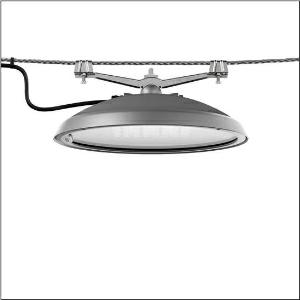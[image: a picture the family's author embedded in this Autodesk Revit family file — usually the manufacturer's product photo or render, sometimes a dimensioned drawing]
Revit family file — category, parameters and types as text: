
# Revit family: dl_r__50_iq_mini___st1_0s_5xa248w41f08he_3a14
name_source: partatom
category: Lighting Fixtures
units: mm (PartAtom-declared; Revit-internal decimal feet)

## family parameters
Cut with Voids When Loaded = No
Host = Face
Light Source = No
Part Type = Normal
Room Calculation Point = No
Round Connector Dimension = Use Diameter
Shared = No

## types (1)
- --- (1 x LED, 9400 lm, 64.6 W, 4000K)
    Apparent Load = 65 VA
    CIE Flux Codes = 37 72 97 100 100
    Color Rendering = 70
    Color Temperature = 4000K
    Default Elevation = 1800 mm
    Description = DL® 50 iQ mini, catenary luminaire, primary light control with lens, of PMMA, primary optical cover: cover, of toughened safety glass, transparent, light distribution: ST1.0s, light emission: direct distribution, primary light characteristic: symmetric, installation type: suspended mounting, LED, High Power LED, rated luminous flux: 9.400lm, luminous efficacy: 146lm/W, light colour: 740, colour temperature: 4000K, control: optimised constant luminous flux control (CLO 2.0), Desk-Remote (wireless, voltage-free reading and setting of iQ features in the workshop via application-optimized NFC function/RFID function), Light-Fading, Smart-Wire, Night-Set, Lumen-Switch, Temp-Guard, Auto-Match, Street-Remote, mains connection: 230..240V, AC, 50/60Hz, start of lifetime: 65W, end of service life: 68W, reduction: 29W, luminaire housing, of diecast aluminium, powder-coated, Siteco® metallic grey (DB 702S), diameter: 500mm, height: 115mm, protection rating (complete): IP66, insulation class (complete): insulation class II (safety insulation), certification: CE, ENEC, VDE, impact resistance: IK08, permissible operating ambient temperature for outdoor applications: -25..+40°C, standard-compliant lighting for roads and squares, packaging unit: 1 piece

Light Distribution: ST1.0s
    Height = 124 mm  [stored 0.406824 ft]
    Lamp = 1 x LED
    Lamp Light Flux = 9400 lm
    Lamp Power = 64.6 W
    Lamp count = 1
    Length = 500 mm
    Luminous efficacy = 146 lm/W
    Manufacturer = Siteco
    ModVariant = No
    Model = 5XA248W41F08HE
    Number of Poles = 1
    OnlyDefault = Yes
    Power Factor = 1
    Product Name = DL® 50 iQ mini | ST1.0s
    Product group = catenary luminaire
    ProductGroupID = 6300
    Protection Class = Protection class II
    Protection Degree = IP 66
    RLX_Detail_Level = 1
    RLX_Emergency_Light_Flux = 0 lm
    RLX_Emergency_Type = 0
    RLX_Emergency_Type_DB = No
    RlxData = <blob elided: 123237 chars, md5=388171ea>
    Socket = socket
    Standby Power = 0 W
    System Light Flux = 9400 lm
    System Power = 65 W
    Type Comments = factory setting: luminous flux: 100 % | dim-lin: 254 | 655 mA
    Type Image = l_1242791.jpg
    URL = http://relux.com
    VarID = @adj_089971
    Voltage = 0 V
    Weight = 0.00 kg
    Width = 0 mm  [stored 0 ft]

note: [stored X ft] marks values corroborated as IEEE doubles in the binary element streams (Revit-internal decimal feet)

## geometry (parser evidence)
native form markers: Blend x4, Sweep x11
no freeform markers — native parametric forms only
